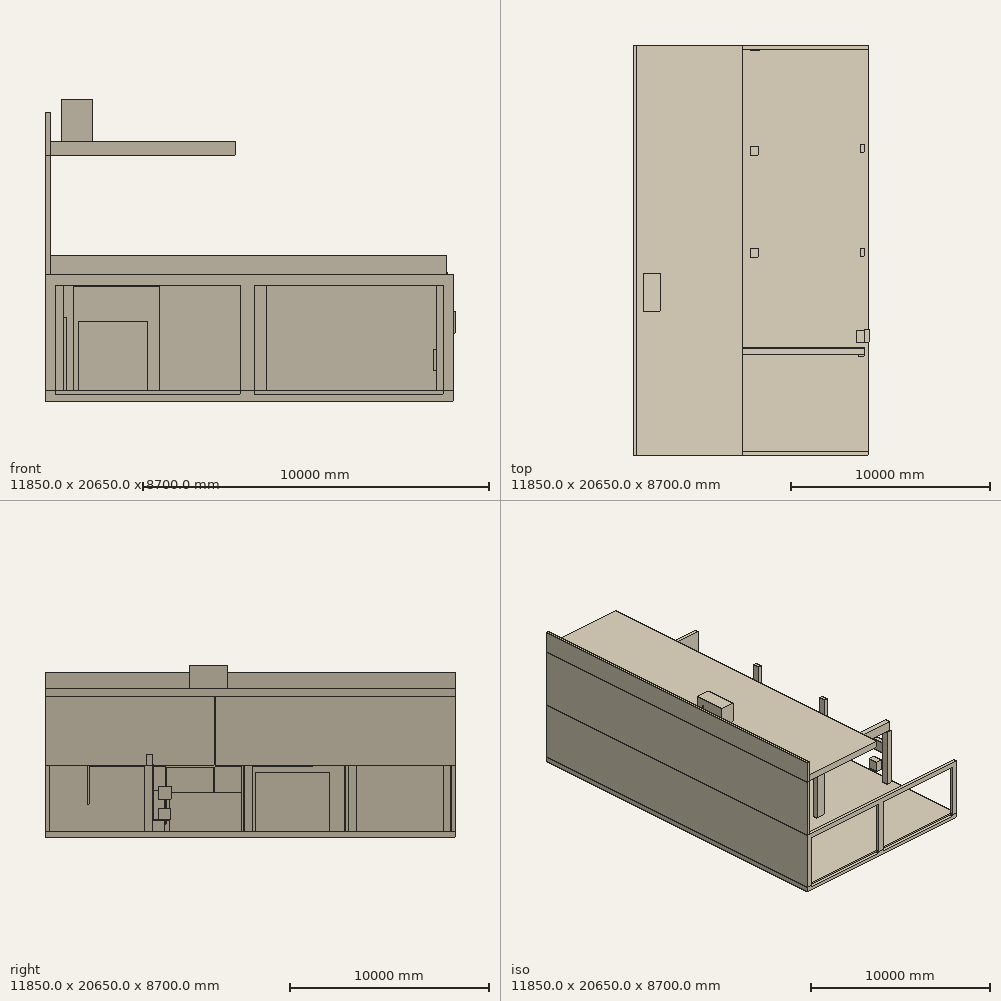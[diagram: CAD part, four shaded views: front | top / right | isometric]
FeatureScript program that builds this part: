
annotation { "Feature Type Name" : "Feature", "Feature Type Description" : "" }
export const myFeature = defineFeature(function(context is Context, id is Id, definition is map)
    precondition{}
    {
        {
            var Q0;
            Q0=qCreatedBy(makeId("Top.planeOp"),FACE);
            var sketch = newSketch(context, id + "F0", { "sketchPlane" : qUnion([Q0])});
            skLineSegment(sketch, "E0.bottom", {"start": v(-5843.2, 9369.94) * mm, "end": v(5956.8, 9369.94) * mm});
            skLineSegment(sketch, "E0.top", {"start": v(-5843.2, -11280.06) * mm, "end": v(5956.8, -11280.06) * mm});
            skLineSegment(sketch, "E0.left", {"start": v(-5843.2, 9369.94) * mm, "end": v(-5843.2, -11280.06) * mm});
            skLineSegment(sketch, "E0.right", {"start": v(5956.8, 9369.94) * mm, "end": v(5956.8, -11280.06) * mm});
            skSolve(sketch);
        }
        {
            var Q0;
            Q0=makeQuery(id+"F0.imprint","IMPRINT",FACE,{"disambiguationData":[TD([[makeQuery(id+"F0.imprint","IMPRINT",EDGE,{"derivedFrom":sQuery(id+"F0.wireOp",EDGE,"E0.bottom")}),-1.0]])]});
            extrude(context, id + "F1", {"entities" : qUnion([Q0]), "oppositeDirection" : true, "depth" : 300 * mm});
        }
        {
            var Q0;
            Q0=makeQuery(id+"F1.opExtrude","CAP_FACE",FACE,{"disambiguationData":[OSD([sQuery(id+"F0.wireOp",EDGE,"E0.bottom"),sQuery(id+"F0.wireOp",EDGE,"E0.top"),sQuery(id+"F0.wireOp",EDGE,"E0.left"),sQuery(id+"F0.wireOp",EDGE,"E0.right")])],"isStart":true});
            var sketch = newSketch(context, id + "F2", { "sketchPlane" : qUnion([Q0])});
            skLineSegment(sketch, "E1.bottom", {"start": v(-5843.2, 9369.94) * mm, "end": v(5956.8, 9369.94) * mm});
            skLineSegment(sketch, "E1.top", {"start": v(-5843.2, -11280.06) * mm, "end": v(5956.8, -11280.06) * mm});
            skLineSegment(sketch, "E1.left", {"start": v(-5843.2, 9369.94) * mm, "end": v(-5843.2, -11280.06) * mm});
            skLineSegment(sketch, "E1.right", {"start": v(5956.8, 9369.94) * mm, "end": v(5956.8, -11280.06) * mm});
            skLineSegment(sketch, "E2.bottom", {"start": v(-5643.2, 9169.94) * mm, "end": v(5756.8, 9169.94) * mm});
            skLineSegment(sketch, "E2.top", {"start": v(-5643.2, -11080.06) * mm, "end": v(5756.8, -11080.06) * mm});
            skLineSegment(sketch, "E2.left", {"start": v(-5643.2, 9169.94) * mm, "end": v(-5643.2, -11080.06) * mm});
            skLineSegment(sketch, "E2.right", {"start": v(5756.8, 9169.94) * mm, "end": v(5756.8, -11080.06) * mm});
            skSolve(sketch);
        }
        {
            var Q0;
            Q0=makeQuery(id+"F2.imprint","IMPRINT",FACE,{"disambiguationData":[TD([[makeQuery(id+"F2.imprint","IMPRINT",EDGE,{"derivedFrom":sQuery(id+"F2.wireOp",EDGE,"E1.bottom")}),-1.0]])]});
            extrude(context, id + "F3", {"entities" : qUnion([Q0]), "depth" : 3350 * mm});
        }
        {
            var Q0;
            Q0=makeQuery(id+"F3.boolean.opBoolean","MERGE",FACE,{"derivedFrom":[makeQuery(id+"F1.opExtrude","SWEPT_FACE",FACE,{"disambiguationData":[OSD([sQuery(id+"F0.wireOp",EDGE,"E0.top")])]}),makeQuery(id+"F3.opExtrude","SWEPT_FACE",FACE,{"disambiguationData":[OSD([sQuery(id+"F2.wireOp",EDGE,"E1.top")])]})]});
            var sketch = newSketch(context, id + "F4", { "sketchPlane" : qUnion([Q0])});
            skLineSegment(sketch, "E3.bottom", {"start": v(-5543.2, 3050) * mm, "end": v(-200, 3050) * mm});
            skLineSegment(sketch, "E3.top", {"start": v(-5543.2, -100) * mm, "end": v(-200, -100) * mm});
            skLineSegment(sketch, "E3.left", {"start": v(-5543.2, 3050) * mm, "end": v(-5543.2, -100) * mm});
            skLineSegment(sketch, "E3.right", {"start": v(-200, 3050) * mm, "end": v(-200, -100) * mm});
            skLineSegment(sketch, "E4.bottom", {"start": v(200, 3050) * mm, "end": v(5656.8, 3050) * mm});
            skLineSegment(sketch, "E4.top", {"start": v(200, -100) * mm, "end": v(5656.8, -100) * mm});
            skLineSegment(sketch, "E4.left", {"start": v(200, 3050) * mm, "end": v(200, -100) * mm});
            skLineSegment(sketch, "E4.right", {"start": v(5656.8, 3050) * mm, "end": v(5656.8, -100) * mm});
            skSolve(sketch);
        }
        {
            var Q0;
            Q0 = qSketchRegion(id + "F4", true);
            extrude(context, id + "F5", {"entities" : qUnion([Q0]), "operationType" : NewBodyOperationType.REMOVE, "oppositeDirection" : true, "depth" : 200 * mm});
        }
        {
            var Q0;
            Q0=makeQuery(id+"F3.opExtrude","CAP_FACE",FACE,{"disambiguationData":[OSD([sQuery(id+"F2.wireOp",EDGE,"E1.bottom"),sQuery(id+"F2.wireOp",EDGE,"E1.top"),sQuery(id+"F2.wireOp",EDGE,"E1.left"),sQuery(id+"F2.wireOp",EDGE,"E1.right"),sQuery(id+"F2.wireOp",EDGE,"E2.bottom"),sQuery(id+"F2.wireOp",EDGE,"E2.top"),sQuery(id+"F2.wireOp",EDGE,"E2.left"),sQuery(id+"F2.wireOp",EDGE,"E2.right")])],"isStart":false});
            var sketch = newSketch(context, id + "F6", { "sketchPlane" : qUnion([Q0])});
            skLineSegment(sketch, "E5.bottom", {"start": v(-5643.2, 9169.94) * mm, "end": v(-5443.2, 9169.94) * mm});
            skLineSegment(sketch, "E5.top", {"start": v(-5643.2, 8769.94) * mm, "end": v(-5443.2, 8769.94) * mm});
            skLineSegment(sketch, "E5.left", {"start": v(-5643.2, 9169.94) * mm, "end": v(-5643.2, 8769.94) * mm});
            skLineSegment(sketch, "E5.right", {"start": v(-5443.2, 9169.94) * mm, "end": v(-5443.2, 8769.94) * mm});
            skLineSegment(sketch, "E6.bottom", {"start": v(-5643.2, 4319.94) * mm, "end": v(-5573.2, 4319.94) * mm});
            skLineSegment(sketch, "E6.top", {"start": v(-5643.2, 3769.94) * mm, "end": v(-5573.2, 3769.94) * mm});
            skLineSegment(sketch, "E6.left", {"start": v(-5643.2, 4319.94) * mm, "end": v(-5643.2, 3769.94) * mm});
            skLineSegment(sketch, "E6.right", {"start": v(-5573.2, 4319.94) * mm, "end": v(-5573.2, 3769.94) * mm});
            skLineSegment(sketch, "E7.bottom", {"start": v(-5643.2, -880.06) * mm, "end": v(-5573.2, -880.06) * mm});
            skLineSegment(sketch, "E7.top", {"start": v(-5643.2, -1430.06) * mm, "end": v(-5573.2, -1430.06) * mm});
            skLineSegment(sketch, "E7.left", {"start": v(-5643.2, -880.06) * mm, "end": v(-5643.2, -1430.06) * mm});
            skLineSegment(sketch, "E7.right", {"start": v(-5573.2, -880.06) * mm, "end": v(-5573.2, -1430.06) * mm});
            skLineSegment(sketch, "E8.bottom", {"start": v(-5643.2, -5900.06) * mm, "end": v(-5323.2, -5900.06) * mm});
            skLineSegment(sketch, "E8.top", {"start": v(-5643.2, -6200.06) * mm, "end": v(-5323.2, -6200.06) * mm});
            skLineSegment(sketch, "E8.left", {"start": v(-5643.2, -5900.06) * mm, "end": v(-5643.2, -6200.06) * mm});
            skLineSegment(sketch, "E8.right", {"start": v(-5323.2, -5900.06) * mm, "end": v(-5323.2, -6200.06) * mm});
            skLineSegment(sketch, "E9.bottom", {"start": v(6.8, 9169.94) * mm, "end": v(556.8, 9169.94) * mm});
            skLineSegment(sketch, "E9.top", {"start": v(6.8, 9099.94) * mm, "end": v(556.8, 9099.94) * mm});
            skLineSegment(sketch, "E9.left", {"start": v(6.8, 9169.94) * mm, "end": v(6.8, 9099.94) * mm});
            skLineSegment(sketch, "E9.right", {"start": v(556.8, 9169.94) * mm, "end": v(556.8, 9099.94) * mm});
            skLineSegment(sketch, "E10.bottom", {"start": v(6.8, -850.06) * mm, "end": v(456.8, -850.06) * mm});
            skLineSegment(sketch, "E10.top", {"start": v(6.8, -1300.06) * mm, "end": v(456.8, -1300.06) * mm});
            skLineSegment(sketch, "E10.left", {"start": v(6.8, -850.06) * mm, "end": v(6.8, -1300.06) * mm});
            skLineSegment(sketch, "E10.right", {"start": v(456.8, -850.06) * mm, "end": v(456.8, -1300.06) * mm});
            skLineSegment(sketch, "E11.bottom", {"start": v(6.8, -5900.06) * mm, "end": v(556.8, -5900.06) * mm});
            skLineSegment(sketch, "E11.top", {"start": v(6.8, -6200.06) * mm, "end": v(556.8, -6200.06) * mm});
            skLineSegment(sketch, "E11.left", {"start": v(6.8, -5900.06) * mm, "end": v(6.8, -6200.06) * mm});
            skLineSegment(sketch, "E11.right", {"start": v(556.8, -5900.06) * mm, "end": v(556.8, -6200.06) * mm});
            skLineSegment(sketch, "E12.bottom", {"start": v(5556.8, -850.06) * mm, "end": v(5756.8, -850.06) * mm});
            skLineSegment(sketch, "E12.top", {"start": v(5556.8, -1250.06) * mm, "end": v(5756.8, -1250.06) * mm});
            skLineSegment(sketch, "E12.left", {"start": v(5556.8, -850.06) * mm, "end": v(5556.8, -1250.06) * mm});
            skLineSegment(sketch, "E12.right", {"start": v(5756.8, -850.06) * mm, "end": v(5756.8, -1250.06) * mm});
            skLineSegment(sketch, "E13.bottom", {"start": v(5456.8, -5900.06) * mm, "end": v(5756.8, -5900.06) * mm});
            skLineSegment(sketch, "E13.top", {"start": v(5456.8, -6300.06) * mm, "end": v(5756.8, -6300.06) * mm});
            skLineSegment(sketch, "E13.left", {"start": v(5456.8, -5900.06) * mm, "end": v(5456.8, -6300.06) * mm});
            skLineSegment(sketch, "E13.right", {"start": v(5756.8, -5900.06) * mm, "end": v(5756.8, -6300.06) * mm});
            skLineSegment(sketch, "E14.bottom", {"start": v(5556.8, 4369.94) * mm, "end": v(5756.8, 4369.94) * mm});
            skLineSegment(sketch, "E14.top", {"start": v(5556.8, 3969.94) * mm, "end": v(5756.8, 3969.94) * mm});
            skLineSegment(sketch, "E14.left", {"start": v(5556.8, 4369.94) * mm, "end": v(5556.8, 3969.94) * mm});
            skLineSegment(sketch, "E14.right", {"start": v(5756.8, 4369.94) * mm, "end": v(5756.8, 3969.94) * mm});
            skLineSegment(sketch, "E15.bottom", {"start": v(6.8, 4299.94) * mm, "end": v(456.8, 4299.94) * mm});
            skLineSegment(sketch, "E15.top", {"start": v(6.8, 3849.94) * mm, "end": v(456.8, 3849.94) * mm});
            skLineSegment(sketch, "E15.left", {"start": v(6.8, 4299.94) * mm, "end": v(6.8, 3849.94) * mm});
            skLineSegment(sketch, "E15.right", {"start": v(456.8, 4299.94) * mm, "end": v(456.8, 3849.94) * mm});
            skSolve(sketch);
        }
        {
            var Q0;
            Q0 = qSketchRegion(id + "F6", true);
            extrude(context, id + "F7", {"entities" : qUnion([Q0]), "endBound" : BoundingType.UP_TO_NEXT, "oppositeDirection" : true, "depth" : 25 * mm});
        }
        {
            var Q0;
            Q0=makeQuery(id+"F3.opExtrude","SWEPT_FACE",FACE,{"disambiguationData":[OSD([sQuery(id+"F2.wireOp",EDGE,"E2.right")])]});
            var sketch = newSketch(context, id + "F8", { "sketchPlane" : qUnion([Q0])});
            skLineSegment(sketch, "E16.bottom", {"start": v(-9169.94, 3350) * mm, "end": v(11080.06, 3350) * mm});
            skLineSegment(sketch, "E16.top", {"start": v(-9169.94, 0) * mm, "end": v(11080.06, 0) * mm});
            skLineSegment(sketch, "E16.left", {"start": v(-9169.94, 3350) * mm, "end": v(-9169.94, 0) * mm});
            skLineSegment(sketch, "E16.right", {"start": v(11080.06, 3350) * mm, "end": v(11080.06, 0) * mm});
            skSolve(sketch);
        }
        {
            var Q0;
            Q0=makeQuery(id+"F8.imprint","IMPRINT",FACE,{"disambiguationData":[TD([[makeQuery(id+"F8.imprint","IMPRINT",EDGE,{"derivedFrom":sQuery(id+"F8.wireOp",EDGE,"E16.bottom")}),-1.0]])]});
            extrude(context, id + "F9", {"entities" : qUnion([Q0]), "operationType" : NewBodyOperationType.REMOVE, "endBound" : BoundingType.THROUGH_ALL, "oppositeDirection" : true, "depth" : 25 * mm});
        }
        {
            var Q0;
            Q0=makeQuery(id+"F3.opExtrude","SWEPT_FACE",FACE,{"disambiguationData":[OSD([sQuery(id+"F2.wireOp",EDGE,"E1.left")])]});
            var sketch = newSketch(context, id + "F10", { "sketchPlane" : qUnion([Q0])});
            skLineSegment(sketch, "E17.bottom", {"start": v(-9369.94, 0) * mm, "end": v(11280.06, 0) * mm});
            skLineSegment(sketch, "E17.top", {"start": v(-9369.94, 6800) * mm, "end": v(11280.06, 6800) * mm});
            skLineSegment(sketch, "E17.left", {"start": v(-9369.94, 0) * mm, "end": v(-9369.94, 6800) * mm});
            skLineSegment(sketch, "E17.right", {"start": v(11280.06, 0) * mm, "end": v(11280.06, 6800) * mm});
            skSolve(sketch);
        }
        {
            var Q0;
            {var subQ0=sQuery(id+"F10.wireOp",EDGE,"E17.top");Q0=makeQuery(id+"F10.imprint","IMPRINT",FACE,{"disambiguationData":[TD([[makeQuery(id+"F10.imprint","IMPRINT",EDGE,{"derivedFrom":subQ0}),-1.0]])]});}
            extrude(context, id + "F11", {"entities" : qUnion([Q0]), "oppositeDirection" : true, "depth" : 150 * mm});
        }
        {
            var Q0;
            Q0=makeQuery(id+"F7.opExtrude","SWEPT_FACE",FACE,{"disambiguationData":[OSD([sQuery(id+"F6.wireOp",EDGE,"E11.top")])]});
            var sketch = newSketch(context, id + "F12", { "sketchPlane" : qUnion([Q0])});
            skLineSegment(sketch, "E18.bottom", {"start": v(-5693.2, 3349.04) * mm, "end": v(5756.8, 3349.04) * mm});
            skLineSegment(sketch, "E18.top", {"start": v(-5693.2, 3899.04) * mm, "end": v(5756.8, 3899.04) * mm});
            skLineSegment(sketch, "E18.left", {"start": v(-5693.2, 3349.04) * mm, "end": v(-5693.2, 3899.04) * mm});
            skLineSegment(sketch, "E18.right", {"start": v(5756.8, 3349.04) * mm, "end": v(5756.8, 3899.04) * mm});
            skSolve(sketch);
        }
        {
            var Q0;
            Q0=makeQuery(id+"F12.imprint","IMPRINT",FACE,{"disambiguationData":[TD([[makeQuery(id+"F12.imprint","IMPRINT",EDGE,{"derivedFrom":sQuery(id+"F12.wireOp",EDGE,"E18.top")}),-1.0]])]});
            extrude(context, id + "F13", {"entities" : qUnion([Q0]), "oppositeDirection" : true, "depth" : 300 * mm});
        }
        {
            var Q0;
            Q0=makeQuery(id+"F11.opExtrude","SWEPT_FACE",FACE,{"disambiguationData":[OSD([sQuery(id+"F10.wireOp",EDGE,"E17.top")])]});
            var sketch = newSketch(context, id + "F14", { "sketchPlane" : qUnion([Q0])});
            skLineSegment(sketch, "E19.bottom", {"start": v(-5843.2, 9369.94) * mm, "end": v(-352.14, 9369.94) * mm});
            skLineSegment(sketch, "E19.top", {"start": v(-5843.2, -11280.06) * mm, "end": v(-352.14, -11280.06) * mm});
            skLineSegment(sketch, "E19.right", {"start": v(-352.14, 9369.94) * mm, "end": v(-352.14, -11280.06) * mm});
            skLineSegment(sketch, "E20", {"start": v(-5843.2, 9369.94) * mm, "end": v(-5843.2, -11280.06) * mm});
            skSolve(sketch);
        }
        {
            var Q0;
            {var subQ2=sQuery(id+"F14.wireOp",EDGE,"E19.right");Q0=makeQuery(id+"F14.imprint","IMPRINT",FACE,{"disambiguationData":[TD([[makeQuery(id+"F14.imprint","IMPRINT",EDGE,{"derivedFrom":subQ2}),-1.0]])]});}
            extrude(context, id + "F15", {"entities" : qUnion([Q0]), "depth" : 400 * mm});
        }
        {
            var Q0;
            Q0=makeQuery(id+"F11.opExtrude","SWEPT_FACE",FACE,{"disambiguationData":[OSD([sQuery(id+"F10.wireOp",EDGE,"E17.top")])]});
            var sketch = newSketch(context, id + "F16", { "sketchPlane" : qUnion([Q0])});
            skLineSegment(sketch, "E21.bottom", {"start": v(-5843.2, 9369.94) * mm, "end": v(-5693.2, 9369.94) * mm});
            skLineSegment(sketch, "E21.top", {"start": v(-5843.2, -11280.06) * mm, "end": v(-5693.2, -11280.06) * mm});
            skLineSegment(sketch, "E21.left", {"start": v(-5843.2, 9369.94) * mm, "end": v(-5843.2, -11280.06) * mm});
            skLineSegment(sketch, "E21.right", {"start": v(-5693.2, 9369.94) * mm, "end": v(-5693.2, -11280.06) * mm});
            skSolve(sketch);
        }
        {
            var Q0;
            Q0 = qSketchRegion(id + "F16", true);
            extrude(context, id + "F17", {"entities" : qUnion([Q0]), "depth" : 1250 * mm});
        }
        {
            var Q0;
            Q0=makeQuery(id+"F3.opExtrude","SWEPT_FACE",FACE,{"disambiguationData":[OSD([sQuery(id+"F2.wireOp",EDGE,"E2.left")])]});
            var sketch = newSketch(context, id + "F18", { "sketchPlane" : qUnion([Q0])});
            skLineSegment(sketch, "E22.bottom", {"start": v(-5880.8, 0) * mm, "end": v(-5280.8, 0) * mm});
            skLineSegment(sketch, "E22.top", {"start": v(-5880.8, 2100) * mm, "end": v(-5280.8, 2100) * mm});
            skLineSegment(sketch, "E22.left", {"start": v(-5880.8, 0) * mm, "end": v(-5880.8, 2100) * mm});
            skLineSegment(sketch, "E22.right", {"start": v(-5280.8, 0) * mm, "end": v(-5280.8, 2100) * mm});
            skSolve(sketch);
        }
        {
            var Q0;
            Q0=makeQuery(id+"F18.imprint","IMPRINT",FACE,{"disambiguationData":[TD([[makeQuery(id+"F18.imprint","IMPRINT",EDGE,{"derivedFrom":sQuery(id+"F18.wireOp",EDGE,"E22.bottom")}),-1.0]])]});
            extrude(context, id + "F19", {"entities" : qUnion([Q0]), "depth" : 400 * mm});
        }
        {
            var Q0;
            Q0=makeQuery(id+"F7.opExtrude","SWEPT_FACE",FACE,{"disambiguationData":[OSD([sQuery(id+"F6.wireOp",EDGE,"E13.right")])]});
            var sketch = newSketch(context, id + "F20", { "sketchPlane" : qUnion([Q0])});
            skLineSegment(sketch, "E23.bottom", {"start": v(-5600.06, 2300) * mm, "end": v(-4950.06, 2300) * mm});
            skLineSegment(sketch, "E23.top", {"start": v(-5600.06, 1650) * mm, "end": v(-4950.06, 1650) * mm});
            skLineSegment(sketch, "E23.left", {"start": v(-5600.06, 2300) * mm, "end": v(-5600.06, 1650) * mm});
            skLineSegment(sketch, "E23.right", {"start": v(-4950.06, 2300) * mm, "end": v(-4950.06, 1650) * mm});
            skSolve(sketch);
        }
        {
            var Q0;
            Q0=makeQuery(id+"F20.imprint","IMPRINT",FACE,{"disambiguationData":[TD([[makeQuery(id+"F20.imprint","IMPRINT",EDGE,{"derivedFrom":sQuery(id+"F20.wireOp",EDGE,"E23.bottom")}),-1.0]])]});
            extrude(context, id + "F21", {"entities" : qUnion([Q0]), "depth" : 250 * mm});
        }
        {
            var Q0;
            Q0=makeQuery(id+"F7.opExtrude","SWEPT_FACE",FACE,{"disambiguationData":[OSD([sQuery(id+"F6.wireOp",EDGE,"E13.right")])]});
            var sketch = newSketch(context, id + "F22", { "sketchPlane" : qUnion([Q0])});
            skLineSegment(sketch, "E24.bottom", {"start": v(-5581.49, 1175.34) * mm, "end": v(-4981.49, 1175.34) * mm});
            skLineSegment(sketch, "E24.top", {"start": v(-5581.49, 575.34) * mm, "end": v(-4981.49, 575.34) * mm});
            skLineSegment(sketch, "E24.left", {"start": v(-5581.49, 1175.34) * mm, "end": v(-5581.49, 575.34) * mm});
            skLineSegment(sketch, "E24.right", {"start": v(-4981.49, 1175.34) * mm, "end": v(-4981.49, 575.34) * mm});
            skSolve(sketch);
        }
        {
            var Q0;
            Q0=makeQuery(id+"F22.imprint","IMPRINT",FACE,{"disambiguationData":[TD([[makeQuery(id+"F22.imprint","IMPRINT",EDGE,{"derivedFrom":sQuery(id+"F22.wireOp",EDGE,"E24.bottom")}),-1.0]])]});
            extrude(context, id + "F23", {"entities" : qUnion([Q0]), "oppositeDirection" : true, "depth" : 400 * mm});
        }
        {
            var Q0;
            Q0=makeQuery(id+"F23.opExtrude","CAP_FACE",FACE,{"disambiguationData":[OSD([sQuery(id+"F22.wireOp",EDGE,"E24.bottom"),sQuery(id+"F22.wireOp",EDGE,"E24.top"),sQuery(id+"F22.wireOp",EDGE,"E24.left"),sQuery(id+"F22.wireOp",EDGE,"E24.right")])],"isStart":true});
            var sketch = newSketch(context, id + "F24", { "sketchPlane" : qUnion([Q0])});
            skLineSegment(sketch, "E25", {"start": v(-4981.49, 575.34) * mm, "end": v(-5903.34, 575.34) * mm});
            skLineSegment(sketch, "E26", {"start": v(-5903.34, 575.34) * mm, "end": v(-5903.34, 3349.1) * mm});
            skLineSegment(sketch, "E27", {"start": v(-5903.34, 3349.1) * mm, "end": v(-5855.06, 3349.1) * mm});
            skLineSegment(sketch, "E28", {"start": v(-5855.06, 3349.1) * mm, "end": v(-5855.06, 635.67) * mm});
            skLineSegment(sketch, "E29", {"start": v(-5855.06, 635.67) * mm, "end": v(-4981.49, 635.67) * mm});
            skLineSegment(sketch, "E30", {"start": v(-4981.49, 635.67) * mm, "end": v(-4981.49, 575.34) * mm});
            skSolve(sketch);
        }
        {
            var Q0;
            {var subQ0=sQuery(id+"F24.wireOp",EDGE,"E26");Q0=makeQuery(id+"F24.imprint","IMPRINT",FACE,{"disambiguationData":[TD([[makeQuery(id+"F24.imprint","IMPRINT",EDGE,{"derivedFrom":subQ0}),-1.0]])]});}
            var Q1;
            {var subQ3=sQuery(id+"F24.wireOp",EDGE,"E30");Q1=makeQuery(id+"F24.imprint","IMPRINT",FACE,{"disambiguationData":[TD([[makeQuery(id+"F24.imprint","IMPRINT",EDGE,{"derivedFrom":subQ3}),-1.0]])]});}
            extrude(context, id + "F25", {"entities" : qUnion([Q0, Q1]), "depth" : 25 * mm});
        }
        {
            var Q0;
            Q0=makeQuery(id+"F25.opExtrude","CAP_FACE",FACE,{"disambiguationData":[OSD([sQuery(id+"F24.wireOp",EDGE,"E25"),sQuery(id+"F24.wireOp",EDGE,"E26"),sQuery(id+"F24.wireOp",EDGE,"E27"),sQuery(id+"F24.wireOp",EDGE,"E28"),sQuery(id+"F24.wireOp",EDGE,"E29"),sQuery(id+"F24.wireOp",EDGE,"E30")])],"isStart":false});
            var sketch = newSketch(context, id + "F26", { "sketchPlane" : qUnion([Q0])});
            skLineSegment(sketch, "E31.bottom", {"start": v(-5903.34, 3349.1) * mm, "end": v(-5855.06, 3349.1) * mm});
            skLineSegment(sketch, "E31.top", {"start": v(-5903.34, 3408.67) * mm, "end": v(-5855.06, 3408.67) * mm});
            skLineSegment(sketch, "E31.left", {"start": v(-5903.34, 3349.1) * mm, "end": v(-5903.34, 3408.67) * mm});
            skLineSegment(sketch, "E31.right", {"start": v(-5855.06, 3349.1) * mm, "end": v(-5855.06, 3408.67) * mm});
            skSolve(sketch);
        }
        {
            var Q0;
            Q0=makeQuery(id+"F26.imprint","IMPRINT",FACE,{"disambiguationData":[TD([[makeQuery(id+"F26.imprint","IMPRINT",EDGE,{"derivedFrom":sQuery(id+"F26.wireOp",EDGE,"E31.bottom")}),1.0]])]});
            var Q1;
            Q1=makeQuery(id+"F11.opExtrude","SWEPT_BODY",BODY,{"disambiguationData":[OSD([sQuery(id+"F2.wireOp",EDGE,"E1.left"),sQuery(id+"F10.wireOp",EDGE,"E17.top"),sQuery(id+"F10.wireOp",EDGE,"E17.left"),sQuery(id+"F10.wireOp",EDGE,"E17.right")])]});
            extrude(context, id + "F27", {"entities" : qUnion([Q0]), "oppositeDirection" : true, "endBoundEntityBody" : qUnion([Q1]), "depth" : 11600 * mm});
        }
        {
            var Q0;
            Q0=makeQuery(id+"F27.opExtrude","SWEPT_FACE",FACE,{"disambiguationData":[OSD([sQuery(id+"F26.wireOp",EDGE,"E31.top")])]});
            var sketch = newSketch(context, id + "F28", { "sketchPlane" : qUnion([Q0])});
            skLineSegment(sketch, "E32.bottom", {"start": v(-5695.69, -5855.06) * mm, "end": v(-5639.24, -5855.06) * mm});
            skLineSegment(sketch, "E32.top", {"start": v(-5695.69, -5901.15) * mm, "end": v(-5639.24, -5901.15) * mm});
            skLineSegment(sketch, "E32.left", {"start": v(-5695.69, -5855.06) * mm, "end": v(-5695.69, -5901.15) * mm});
            skLineSegment(sketch, "E32.right", {"start": v(-5639.24, -5855.06) * mm, "end": v(-5639.24, -5901.15) * mm});
            skSolve(sketch);
        }
        {
            var Q0;
            Q0=makeQuery(id+"F28.imprint","IMPRINT",FACE,{"disambiguationData":[TD([[makeQuery(id+"F28.imprint","IMPRINT",EDGE,{"derivedFrom":sQuery(id+"F28.wireOp",EDGE,"E32.bottom")}),-1.0]])]});
            extrude(context, id + "F29", {"entities" : qUnion([Q0]), "oppositeDirection" : true, "depth" : 3000 * mm});
        }
        {
            var Q0;
            Q0=makeQuery(id+"F3.opExtrude","SWEPT_FACE",FACE,{"disambiguationData":[OSD([sQuery(id+"F2.wireOp",EDGE,"E2.left")])]});
            var sketch = newSketch(context, id + "F30", { "sketchPlane" : qUnion([Q0])});
            skLineSegment(sketch, "E33", {"start": v(-5259.35, 350) * mm, "end": v(-5259.35, 3350) * mm});
            skLineSegment(sketch, "E34", {"start": v(-5259.35, 3350) * mm, "end": v(-2759.35, 3350) * mm});
            skLineSegment(sketch, "E35", {"start": v(-2759.35, 3350) * mm, "end": v(-2759.35, 1350) * mm});
            skLineSegment(sketch, "E36", {"start": v(-5259.35, 350) * mm, "end": v(-5161.18, 350) * mm});
            skLineSegment(sketch, "E37", {"start": v(-5161.18, 350) * mm, "end": v(-5161.18, 3273.45) * mm});
            skLineSegment(sketch, "E38", {"start": v(-5161.18, 3273.45) * mm, "end": v(-2834.37, 3273.45) * mm});
            skLineSegment(sketch, "E39", {"start": v(-2834.37, 3273.45) * mm, "end": v(-2834.37, 1350) * mm});
            skLineSegment(sketch, "E40", {"start": v(-2834.37, 1350) * mm, "end": v(-2759.35, 1350) * mm});
            skSolve(sketch);
        }
        {
            var Q0;
            Q0=makeQuery(id+"F30.imprint","IMPRINT",FACE,{"disambiguationData":[TD([[makeQuery(id+"F30.imprint","IMPRINT",EDGE,{"derivedFrom":sQuery(id+"F30.wireOp",EDGE,"E33")}),-1.0]])]});
            extrude(context, id + "F31", {"entities" : qUnion([Q0]), "depth" : 25 * mm});
        }
        {
            var Q0;
            Q0=makeQuery(id+"F31.opExtrude","CAP_FACE",FACE,{"disambiguationData":[OSD([sQuery(id+"F30.wireOp",EDGE,"E33"),sQuery(id+"F30.wireOp",EDGE,"E34"),sQuery(id+"F30.wireOp",EDGE,"E35"),sQuery(id+"F30.wireOp",EDGE,"E36"),sQuery(id+"F30.wireOp",EDGE,"E37"),sQuery(id+"F30.wireOp",EDGE,"E38"),sQuery(id+"F30.wireOp",EDGE,"E39"),sQuery(id+"F30.wireOp",EDGE,"E40")])],"isStart":false});
            var sketch = newSketch(context, id + "F32", { "sketchPlane" : qUnion([Q0])});
            skLineSegment(sketch, "E41", {"start": v(-5259.35, 350) * mm, "end": v(-5259.35, 3350) * mm});
            skLineSegment(sketch, "E42", {"start": v(-5259.35, 3350) * mm, "end": v(2240.65, 3350) * mm});
            skLineSegment(sketch, "E43", {"start": v(2240.65, 3350) * mm, "end": v(2240.65, 1350) * mm});
            skLineSegment(sketch, "E44", {"start": v(-5259.35, 350) * mm, "end": v(-5161.18, 350) * mm});
            skLineSegment(sketch, "E45", {"start": v(-5161.18, 350) * mm, "end": v(-5161.18, 3273.45) * mm});
            skLineSegment(sketch, "E46", {"start": v(-5161.18, 3273.45) * mm, "end": v(2205.65, 3273.45) * mm});
            skLineSegment(sketch, "E47", {"start": v(2205.65, 3273.45) * mm, "end": v(2205.65, 1350) * mm});
            skLineSegment(sketch, "E48", {"start": v(2205.65, 1350) * mm, "end": v(2240.65, 1350) * mm});
            skSolve(sketch);
        }
        {
            var Q0;
            {var subQ0=sQuery(id+"F32.wireOp",EDGE,"E43");Q0=makeQuery(id+"F32.imprint","IMPRINT",FACE,{"disambiguationData":[TD([[makeQuery(id+"F32.imprint","IMPRINT",EDGE,{"derivedFrom":subQ0}),-1.0]])]});}
            var Q1;
            {var subQ1=sQuery(id+"F32.wireOp",EDGE,"E41");Q1=makeQuery(id+"F32.imprint","IMPRINT",FACE,{"disambiguationData":[TD([[makeQuery(id+"F32.imprint","IMPRINT",EDGE,{"derivedFrom":subQ1}),-1.0]])]});}
            extrude(context, id + "F33", {"entities" : qUnion([Q0, Q1]), "depth" : 25 * mm});
        }
        {
            var Q0;
            Q0=makeQuery(id+"F33.opExtrude","CAP_FACE",FACE,{"disambiguationData":[OSD([sQuery(id+"F32.wireOp",EDGE,"E41"),sQuery(id+"F32.wireOp",EDGE,"E42"),sQuery(id+"F32.wireOp",EDGE,"E43"),sQuery(id+"F32.wireOp",EDGE,"E44"),sQuery(id+"F32.wireOp",EDGE,"E45"),sQuery(id+"F32.wireOp",EDGE,"E46"),sQuery(id+"F32.wireOp",EDGE,"E47"),sQuery(id+"F32.wireOp",EDGE,"E48")])],"isStart":false});
            var sketch = newSketch(context, id + "F34", { "sketchPlane" : qUnion([Q0])});
            skLineSegment(sketch, "E49", {"start": v(-9053.26, 3273.45) * mm, "end": v(-9053.26, 1357.54) * mm});
            skLineSegment(sketch, "E50", {"start": v(-9053.26, 1357.54) * mm, "end": v(-9161.17, 1357.54) * mm});
            skLineSegment(sketch, "E51", {"start": v(-9161.17, 1357.54) * mm, "end": v(-9161.17, 3357.54) * mm});
            skLineSegment(sketch, "E52", {"start": v(-9161.17, 3357.54) * mm, "end": v(-5161.18, 3350) * mm});
            skLineSegment(sketch, "E53", {"start": v(-5161.18, 350) * mm, "end": v(-5259.35, 350) * mm});
            skLineSegment(sketch, "E54", {"start": v(-5259.35, 350) * mm, "end": v(-5259.35, 3273.45) * mm});
            skLineSegment(sketch, "E55", {"start": v(-5161.18, 350) * mm, "end": v(-5161.18, 401.83) * mm});
            skLineSegment(sketch, "E56", {"start": v(-5161.18, 3350) * mm, "end": v(-5161.18, 401.83) * mm});
            skLineSegment(sketch, "E57", {"start": v(-9053.26, 3273.45) * mm, "end": v(-5259.35, 3273.45) * mm});
            skSolve(sketch);
        }
        {
            var Q0;
            Q0 = qSketchRegion(id + "F34", true);
            extrude(context, id + "F35", {"entities" : qUnion([Q0]), "depth" : 25 * mm});
        }
        {
            var Q0;
            Q0=makeQuery(id+"F35.opExtrude","CAP_FACE",FACE,{"disambiguationData":[OSD([sQuery(id+"F34.wireOp",EDGE,"E49"),sQuery(id+"F34.wireOp",EDGE,"E50"),sQuery(id+"F34.wireOp",EDGE,"E51"),sQuery(id+"F34.wireOp",EDGE,"E52"),sQuery(id+"F34.wireOp",EDGE,"E53"),sQuery(id+"F34.wireOp",EDGE,"E54"),sQuery(id+"F34.wireOp",EDGE,"E55"),sQuery(id+"F34.wireOp",EDGE,"E56"),sQuery(id+"F34.wireOp",EDGE,"E57")])],"isStart":false});
            var sketch = newSketch(context, id + "F36", { "sketchPlane" : qUnion([Q0])});
            skLineSegment(sketch, "E58", {"start": v(-5259.35, 350) * mm, "end": v(-5259.35, 3350.19) * mm});
            skLineSegment(sketch, "E59", {"start": v(-5259.35, 3350.19) * mm, "end": v(-2759.35, 3350.19) * mm});
            skLineSegment(sketch, "E60", {"start": v(-2759.35, 3350.19) * mm, "end": v(-2759.35, 8150.19) * mm});
            skLineSegment(sketch, "E61", {"start": v(-2759.35, 8150.19) * mm, "end": v(-2694.7, 8150.19) * mm});
            skLineSegment(sketch, "E62", {"start": v(-2694.7, 8150.19) * mm, "end": v(-2694.7, 3268.63) * mm});
            skLineSegment(sketch, "E63", {"start": v(-2694.7, 3268.63) * mm, "end": v(-5161.18, 3268.63) * mm});
            skLineSegment(sketch, "E64", {"start": v(-5161.18, 3268.63) * mm, "end": v(-5161.18, 350) * mm});
            skLineSegment(sketch, "E65", {"start": v(-5161.18, 350) * mm, "end": v(-5259.35, 350) * mm});
            skSolve(sketch);
        }
        {
            var Q0;
            {var subQ0=sQuery(id+"F36.wireOp",EDGE,"E59");Q0=makeQuery(id+"F36.imprint","IMPRINT",FACE,{"disambiguationData":[TD([[makeQuery(id+"F36.imprint","IMPRINT",EDGE,{"derivedFrom":subQ0}),-1.0]])]});}
            var Q1;
            {var subQ0=sQuery(id+"F36.wireOp",EDGE,"E64");Q1=makeQuery(id+"F36.imprint","IMPRINT",FACE,{"disambiguationData":[TD([[makeQuery(id+"F36.imprint","IMPRINT",EDGE,{"derivedFrom":subQ0}),-1.0]])]});}
            extrude(context, id + "F37", {"entities" : qUnion([Q0, Q1]), "depth" : 25 * mm});
        }
        {
            var Q0;
            Q0=makeQuery(id+"F1.opExtrude","CAP_FACE",FACE,{"disambiguationData":[OSD([sQuery(id+"F0.wireOp",EDGE,"E0.bottom"),sQuery(id+"F0.wireOp",EDGE,"E0.top"),sQuery(id+"F0.wireOp",EDGE,"E0.left"),sQuery(id+"F0.wireOp",EDGE,"E0.right")])],"isStart":true});
            var sketch = newSketch(context, id + "F38", { "sketchPlane" : qUnion([Q0])});
            skLineSegment(sketch, "E66.bottom", {"start": v(-5043.2, 3009.13) * mm, "end": v(-2543.2, 3009.13) * mm});
            skLineSegment(sketch, "E66.top", {"start": v(-5043.2, -690.87) * mm, "end": v(-2543.2, -690.87) * mm});
            skLineSegment(sketch, "E66.left", {"start": v(-5043.2, 3009.13) * mm, "end": v(-5043.2, -690.87) * mm});
            skLineSegment(sketch, "E66.right", {"start": v(-2543.2, 3009.13) * mm, "end": v(-2543.2, -690.87) * mm});
            skSolve(sketch);
        }
        {
            var Q0;
            Q0 = qSketchRegion(id + "F38", true);
            extrude(context, id + "F39", {"entities" : qUnion([Q0]), "depth" : 3000 * mm});
        }
        {
            var Q0;
            Q0=makeQuery(id+"F1.opExtrude","CAP_FACE",FACE,{"disambiguationData":[OSD([sQuery(id+"F0.wireOp",EDGE,"E0.bottom"),sQuery(id+"F0.wireOp",EDGE,"E0.top"),sQuery(id+"F0.wireOp",EDGE,"E0.left"),sQuery(id+"F0.wireOp",EDGE,"E0.right")])],"isStart":true});
            var sketch = newSketch(context, id + "F40", { "sketchPlane" : qUnion([Q0])});
            skLineSegment(sketch, "E67.bottom", {"start": v(-4894.57, -1427.54) * mm, "end": v(-2894.57, -1427.54) * mm});
            skLineSegment(sketch, "E67.top", {"start": v(-4894.57, -5027.54) * mm, "end": v(-2894.57, -5027.54) * mm});
            skLineSegment(sketch, "E67.left", {"start": v(-4894.57, -1427.54) * mm, "end": v(-4894.57, -5027.54) * mm});
            skLineSegment(sketch, "E67.right", {"start": v(-2894.57, -1427.54) * mm, "end": v(-2894.57, -5027.54) * mm});
            skSolve(sketch);
        }
        {
            var Q0;
            Q0 = qSketchRegion(id + "F40", true);
            extrude(context, id + "F41", {"entities" : qUnion([Q0]), "depth" : 2000 * mm});
        }
        {
            var Q0;
            Q0=makeQuery(id+"F15.opExtrude","CAP_FACE",FACE,{"disambiguationData":[OSD([sQuery(id+"F10.wireOp",EDGE,"E17.top"),sQuery(id+"F14.wireOp",EDGE,"E19.bottom"),sQuery(id+"F14.wireOp",EDGE,"E19.top"),sQuery(id+"F14.wireOp",EDGE,"E19.right")])],"isStart":false});
            var sketch = newSketch(context, id + "F42", { "sketchPlane" : qUnion([Q0])});
            skLineSegment(sketch, "E68.bottom", {"start": v(-5378.13, -2121.75) * mm, "end": v(-4493.5, -2121.75) * mm});
            skLineSegment(sketch, "E68.top", {"start": v(-5378.13, -4049.59) * mm, "end": v(-4493.5, -4049.59) * mm});
            skLineSegment(sketch, "E68.left", {"start": v(-5378.13, -2121.75) * mm, "end": v(-5378.13, -4049.59) * mm});
            skLineSegment(sketch, "E68.right", {"start": v(-4493.5, -2121.75) * mm, "end": v(-4493.5, -4049.59) * mm});
            skSolve(sketch);
        }
        {
            var Q0;
            Q0 = qSketchRegion(id + "F42", true);
            extrude(context, id + "F43", {"entities" : qUnion([Q0]), "depth" : 1200 * mm});
        }
    });
